# Revit family: DockLeveler_XDS-Series_BlueGiant
name_source: partatom
category: Specialty Equipment
units: mm (PartAtom-declared; Revit-internal decimal feet)

## family parameters
Cut with Voids When Loaded = No
Enable Cutting in Views = No
Host = Face
Maintain Annotation Orientation = No
Part Type = Normal
Room Calculation Point = No
Round Connector Dimension = Use Diameter
Shared = No

## types (1)
- DockLeveler_XDS-Series_BlueGiant
    Assembly Code = E1030300
    Available Options = as Specified
    Capacity = as Specified
    Construction Details = http://www.arcat.com
    Default Elevation = 0' - 0"
    Description = Blue Giant Loading Dock Equipment as Specified
    Expected Lifespan (Years) = 0
    Green Building-LEED = http://www.arcat.com
    Installation-Fabrication = http://www.bluegiant.com
    Keynote = 11600
    Lip Inset = 0' - 0"
    Maintenance Schedule (Months) = 0
    Manufacturer = Blue Giant Equipment Corp.
    Manufacturer Fax = 905-457-2313
    Manufacturer Website = http://www.bluegiant.com
    Model = As Specified
    Pit Depth = 1' - 8"
    Pit Length = 5' - 1 1/4"
    Pit Width = 6' - 2"
    Product Data = http://www.arcat.com
    Rear Pit Offset = 0' - 0 1/2"
    Revision = R1_06_2014
    Sales Information = http://www.bluegiant.com
    Send Message = http://www.arcat.com
    SpecWizard = http://www.arcat.com
    Specification = http://www.arcat.com
    URL = http://www.bluegiant.com
    Unit Width = 6' - 0"
    Warranty Duration (Years) = 0

## geometry (parser evidence)
native form markers: Blend x6, Sweep x2
no freeform markers — native parametric forms only
